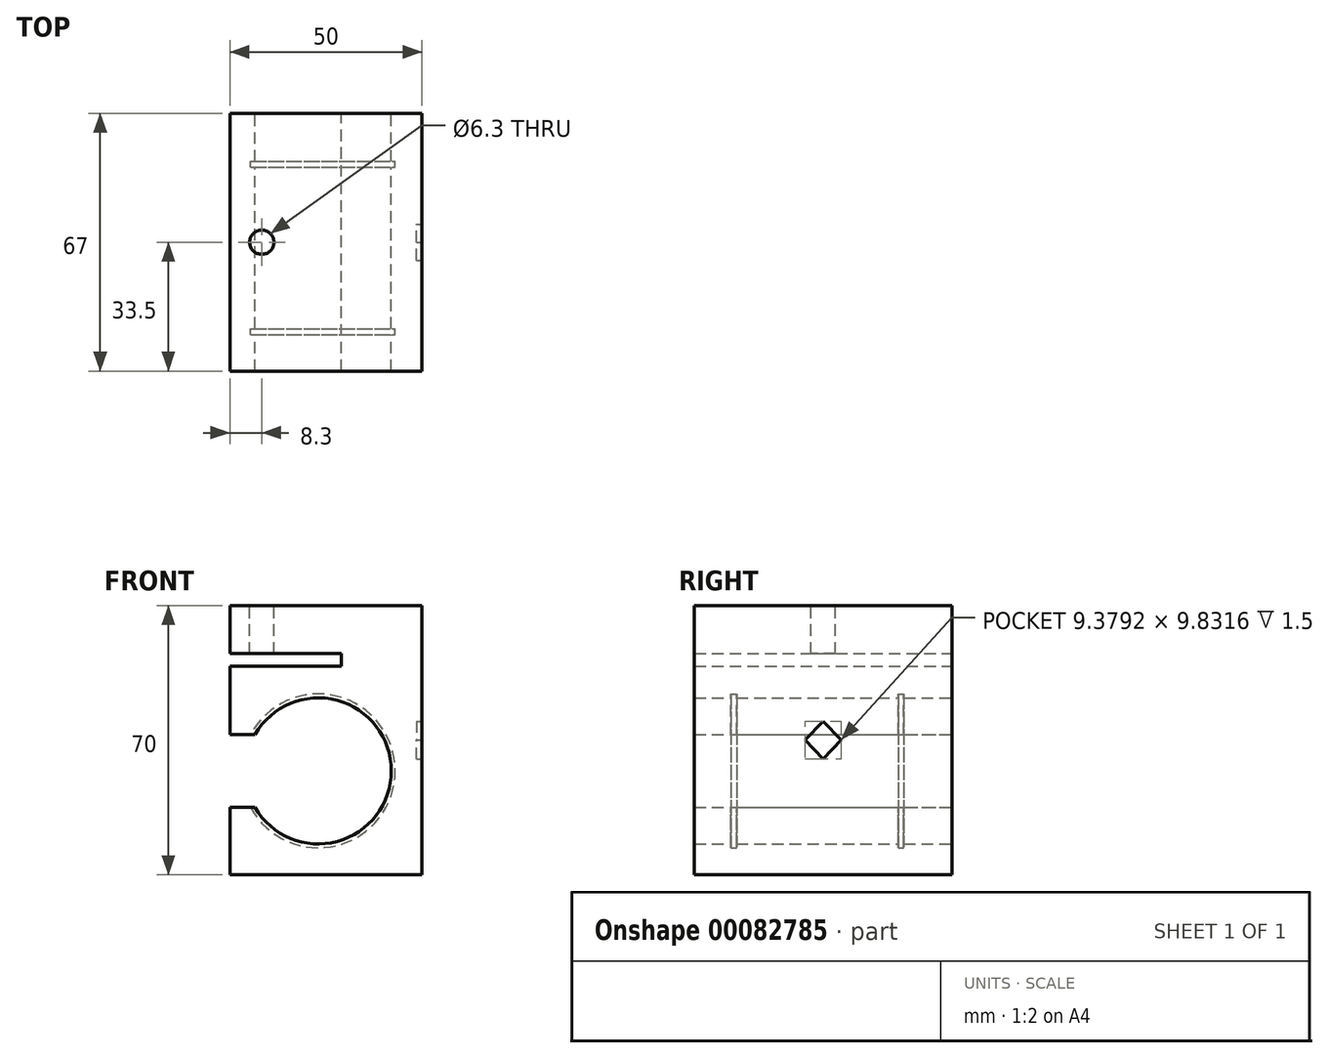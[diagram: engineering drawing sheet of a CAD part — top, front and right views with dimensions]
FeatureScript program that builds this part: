
annotation { "Feature Type Name" : "Feature", "Feature Type Description" : "" }
export const myFeature = defineFeature(function(context is Context, id is Id, definition is map)
    precondition{}
    {
        {
            var Q0;
            Q0=qCreatedBy(makeId("Front.planeOp"),FACE);
            var sketch = newSketch(context, id + "F0", { "sketchPlane" : qUnion([Q0])});
            skLineSegment(sketch, "E0.bottom", {"start": v(0, 0) * mm, "end": v(-50, 0) * mm});
            skLineSegment(sketch, "E0.top", {"start": v(0, 70) * mm, "end": v(-50, 70) * mm});
            skLineSegment(sketch, "E0.left", {"start": v(0, 0) * mm, "end": v(0, 70) * mm});
            skLineSegment(sketch, "E0.right", {"start": v(-50, 0) * mm, "end": v(-50, 70) * mm});
            skSolve(sketch);
        }
        {
            var Q0;
            Q0=makeQuery(id+"F0.imprint","IMPRINT",FACE,{"disambiguationData":[TD([[makeQuery(id+"F0.imprint","IMPRINT",EDGE,{"derivedFrom":sQuery(id+"F0.wireOp",EDGE,"E0.bottom")}),-1.0]])]});
            extrude(context, id + "F1", {"entities" : qUnion([Q0]), "depth" : 67 * mm});
        }
        {
            var Q0;
            Q0=makeQuery(id+"F1.opExtrude","SWEPT_FACE",FACE,{"disambiguationData":[OSD([sQuery(id+"F0.wireOp",EDGE,"E0.left")])]});
            var sketch = newSketch(context, id + "F2", { "sketchPlane" : qUnion([Q0])});
            skLineSegment(sketch, "E1.0", {"start": v(-67, 0) * mm, "end": v(-67, 70) * mm});
            skLineSegment(sketch, "E1.1", {"start": v(-67, 70) * mm, "end": v(0, 70) * mm});
            skLineSegment(sketch, "E1.2", {"start": v(0, 0) * mm, "end": v(0, 70) * mm});
            skLineSegment(sketch, "E1.3", {"start": v(-67, 0) * mm, "end": v(0, 0) * mm});
            skLineSegment(sketch, "E2", {"start": v(-62.2, 70) * mm, "end": v(0, 4.8) * mm});
            skLineSegment(sketch, "E3", {"start": v(0, 4.8) * mm, "end": v(0, 0) * mm});
            skLineSegment(sketch, "E4", {"start": v(-4.8, 0) * mm, "end": v(-67, 65.2) * mm});
            skLineSegment(sketch, "E5", {"start": v(-67, 65.2) * mm, "end": v(-67, 70) * mm});
            skLineSegment(sketch, "E6", {"start": v(-67, 4.8) * mm, "end": v(-4.8, 70) * mm});
            skLineSegment(sketch, "E7", {"start": v(-4.8, 70) * mm, "end": v(0, 70) * mm});
            skLineSegment(sketch, "E8", {"start": v(0, 65.2) * mm, "end": v(-62.2, 0) * mm});
            skLineSegment(sketch, "E9", {"start": v(-62.2, 0) * mm, "end": v(-67, 0) * mm});
            skSolve(sketch);
        }
        {
            var Q0;
            {var subQ0=sQuery(id+"F2.wireOp",EDGE,"E5");Q0=makeQuery(id+"F2.imprint","IMPRINT",FACE,{"disambiguationData":[TD([[makeQuery(id+"F2.imprint","IMPRINT",EDGE,{"derivedFrom":subQ0}),-1.0]])]});}
            var Q1;
            {var subQ0=sQuery(id+"F2.wireOp",EDGE,"E6");var subQ1=sQuery(id+"F2.wireOp",EDGE,"E2");var subQ2=makeQuery(id+"F2.imprint","INTERSECT",VERTEX,{"derivedFrom":[subQ1,subQ0]});Q1=makeQuery(id+"F2.imprint","IMPRINT",FACE,{"disambiguationData":[TD([[makeQuery(id+"F2.imprint","IMPRINT",EDGE,{"disambiguationData":[TD([[subQ2,-1.0]])],"derivedFrom":subQ1}),-1.0]])]});}
            var Q2;
            {var subQ0=sQuery(id+"F2.wireOp",EDGE,"E9");Q2=makeQuery(id+"F2.imprint","IMPRINT",FACE,{"disambiguationData":[TD([[makeQuery(id+"F2.imprint","IMPRINT",EDGE,{"derivedFrom":subQ0}),1.0]])]});}
            var Q3;
            {var subQ0=sQuery(id+"F2.wireOp",EDGE,"E7");Q3=makeQuery(id+"F2.imprint","IMPRINT",FACE,{"disambiguationData":[TD([[makeQuery(id+"F2.imprint","IMPRINT",EDGE,{"derivedFrom":subQ0}),-1.0]])]});}
            var Q4;
            {var subQ0=sQuery(id+"F2.wireOp",EDGE,"E3");Q4=makeQuery(id+"F2.imprint","IMPRINT",FACE,{"disambiguationData":[TD([[makeQuery(id+"F2.imprint","IMPRINT",EDGE,{"derivedFrom":subQ0}),1.0]])]});}
            extrude(context, id + "F3", {"entities" : qUnion([Q0, Q1, Q2, Q3, Q4]), "operationType" : NewBodyOperationType.REMOVE, "oppositeDirection" : true, "depth" : 1.5 * mm});
        }
        {
            var Q0;
            Q0=makeQuery(id+"F1.opExtrude","CAP_FACE",FACE,{"disambiguationData":[OSD([sQuery(id+"F0.wireOp",EDGE,"E0.bottom"),sQuery(id+"F0.wireOp",EDGE,"E0.top"),sQuery(id+"F0.wireOp",EDGE,"E0.left"),sQuery(id+"F0.wireOp",EDGE,"E0.right")])],"isStart":true});
            var sketch = newSketch(context, id + "F4", { "sketchPlane" : qUnion([Q0])});
            skLineSegment(sketch, "E10.0", {"start": v(1.5, 70) * mm, "end": v(50, 70) * mm});
            skLineSegment(sketch, "E10.1", {"start": v(0, 4.8) * mm, "end": v(0, 65.2) * mm});
            skLineSegment(sketch, "E10.2", {"start": v(50, 0) * mm, "end": v(50, 70) * mm});
            skLineSegment(sketch, "E10.3", {"start": v(1.5, 0) * mm, "end": v(50, 0) * mm});
            skLineSegment(sketch, "E11", {"start": v(50, 57.5) * mm, "end": v(21, 57.5) * mm});
            skLineSegment(sketch, "E12", {"start": v(21, 57.5) * mm, "end": v(21, 54.2) * mm});
            skLineSegment(sketch, "E13", {"start": v(21, 54.2) * mm, "end": v(50, 54.2) * mm});
            skCircle(sketch, "E14", {"center": v(27, 27) * mm, "radius": 19 * mm});
            skLineSegment(sketch, "E15", {"start": v(27, 27) * mm, "end": v(110.14, 27) * mm, "construction": true});
            skLineSegment(sketch, "E16", {"start": v(43.45, 17.5) * mm, "end": v(50, 17.5) * mm});
            skLineSegment(sketch, "E17.MirrorCS", {"start": v(43.45, 36.5) * mm, "end": v(50, 36.5) * mm});
            skSolve(sketch);
        }
        {
            var Q0;
            {var subQ0=sQuery(id+"F4.wireOp",EDGE,"E11");Q0=makeQuery(id+"F4.imprint","IMPRINT",FACE,{"disambiguationData":[TD([[makeQuery(id+"F4.imprint","IMPRINT",EDGE,{"derivedFrom":subQ0}),1.0]])]});}
            var Q1;
            {var subQ0=sQuery(id+"F4.wireOp",EDGE,"E14");var subQ1=makeQuery(id+"F4.imprint","INTERSECT",VERTEX,{"derivedFrom":[subQ0,sQuery(id+"F4.wireOp",EDGE,"E16")]});Q1=makeQuery(id+"F4.imprint","IMPRINT",FACE,{"disambiguationData":[TD([[makeQuery(id+"F4.imprint","IMPRINT",EDGE,{"disambiguationData":[TD([[subQ1,1.0]])],"derivedFrom":subQ0}),1.0]])]});}
            var Q2;
            {var subQ0=sQuery(id+"F4.wireOp",EDGE,"E16");Q2=makeQuery(id+"F4.imprint","IMPRINT",FACE,{"disambiguationData":[TD([[makeQuery(id+"F4.imprint","IMPRINT",EDGE,{"derivedFrom":subQ0}),1.0]])]});}
            extrude(context, id + "F5", {"entities" : qUnion([Q0, Q1, Q2]), "operationType" : NewBodyOperationType.REMOVE, "endBound" : BoundingType.THROUGH_ALL, "oppositeDirection" : true, "depth" : 25 * mm});
        }
        {
            var Q0;
            Q0=makeQuery(id+"F1.opExtrude","CAP_FACE",FACE,{"disambiguationData":[OSD([sQuery(id+"F0.wireOp",EDGE,"E0.bottom"),sQuery(id+"F0.wireOp",EDGE,"E0.top"),sQuery(id+"F0.wireOp",EDGE,"E0.left"),sQuery(id+"F0.wireOp",EDGE,"E0.right")])],"isStart":true});
            cPlane(context, id + "F6", {"entities" : qUnion([Q0]), "cplaneType" : CPlaneType.OFFSET, "offset" : 12.5 * mm, "oppositeDirection" : true, "width" : 150 * mm, "height" : 150 * mm});
        }
        {
            var Q0;
            Q0=qCreatedBy(id+"F6.planeOp",FACE);
            var sketch = newSketch(context, id + "F7", { "sketchPlane" : qUnion([Q0])});
            skArc(sketch, "E18.0", {"start": v(43.45, 36.5) * mm, "mid": v(8, 27) * mm, "end": v(43.45, 17.5) * mm});
            skCircle(sketch, "E19", {"center": v(27, 27) * mm, "radius": 20 * mm});
            skSolve(sketch);
        }
        {
            var Q0;
            Q0=makeQuery(id+"F7.imprint","IMPRINT",FACE,{"disambiguationData":[TD([[makeQuery(id+"F7.imprint","IMPRINT",EDGE,{"derivedFrom":sQuery(id+"F7.wireOp",EDGE,"E19")}),1.0]])]});
            extrude(context, id + "F8", {"entities" : qUnion([Q0]), "operationType" : NewBodyOperationType.REMOVE, "oppositeDirection" : true, "depth" : 1.5 * mm});
        }
        {
            var Q0;
            Q0=makeQuery(id+"F8.boolean.opBoolean","COPY",FACE,{"derivedFrom":makeQuery(id+"F8.opExtrude","CAP_FACE",FACE,{"disambiguationData":[OSD([sQuery(id+"F7.wireOp",EDGE,"E19")])],"isStart":false})});
            cPlane(context, id + "F9", {"entities" : qUnion([Q0]), "cplaneType" : CPlaneType.OFFSET, "offset" : 42 * mm, "oppositeDirection" : true, "width" : 150 * mm, "height" : 150 * mm});
        }
        {
            var Q0;
            Q0=qCreatedBy(id+"F9.planeOp",FACE);
            var sketch = newSketch(context, id + "F10", { "sketchPlane" : qUnion([Q0])});
            skArc(sketch, "E20.0", {"start": v(43.45, 17.5) * mm, "mid": v(8, 27) * mm, "end": v(43.45, 36.5) * mm});
            skCircle(sketch, "E21", {"center": v(27, 27) * mm, "radius": 20 * mm});
            skSolve(sketch);
        }
        {
            var Q0;
            Q0=makeQuery(id+"F10.imprint","IMPRINT",FACE,{"disambiguationData":[TD([[makeQuery(id+"F10.imprint","IMPRINT",EDGE,{"derivedFrom":sQuery(id+"F10.wireOp",EDGE,"E21")}),1.0]])]});
            extrude(context, id + "F11", {"entities" : qUnion([Q0]), "operationType" : NewBodyOperationType.REMOVE, "oppositeDirection" : true, "depth" : 1.5 * mm});
        }
        {
            var Q0;
            Q0=makeQuery(id+"F1.opExtrude","SWEPT_FACE",FACE,{"disambiguationData":[OSD([sQuery(id+"F0.wireOp",EDGE,"E0.top")])]});
            var sketch = newSketch(context, id + "F12", { "sketchPlane" : qUnion([Q0])});
            skLineSegment(sketch, "E22.0", {"start": v(-1.5, -67) * mm, "end": v(-50, -67) * mm});
            skLineSegment(sketch, "E22.1", {"start": v(-50, -67) * mm, "end": v(-50, 0) * mm});
            skLineSegment(sketch, "E22.2", {"start": v(-1.5, 0) * mm, "end": v(-50, 0) * mm});
            skLineSegment(sketch, "E22.3", {"start": v(0, -62.2) * mm, "end": v(0, -4.8) * mm});
            skCircle(sketch, "E23", {"center": v(-41.7, -33.5) * mm, "radius": 3.15 * mm});
            skSolve(sketch);
        }
        {
            var Q0;
            Q0=makeQuery(id+"F12.imprint","IMPRINT",FACE,{"disambiguationData":[TD([[makeQuery(id+"F12.imprint","IMPRINT",EDGE,{"derivedFrom":sQuery(id+"F12.wireOp",EDGE,"E23")}),1.0]])]});
            var Q1;
            Q1=makeQuery(id+"F5.boolean.opBoolean","COPY",FACE,{"derivedFrom":makeQuery(id+"F5.opExtrude","SWEPT_FACE",FACE,{"disambiguationData":[OSD([sQuery(id+"F4.wireOp",EDGE,"E11")])]})});
            extrude(context, id + "F13", {"entities" : qUnion([Q0]), "operationType" : NewBodyOperationType.REMOVE, "endBound" : BoundingType.UP_TO_SURFACE, "oppositeDirection" : true, "endBoundEntityFace" : qUnion([Q1]), "depth" : 25 * mm});
        }
    });
